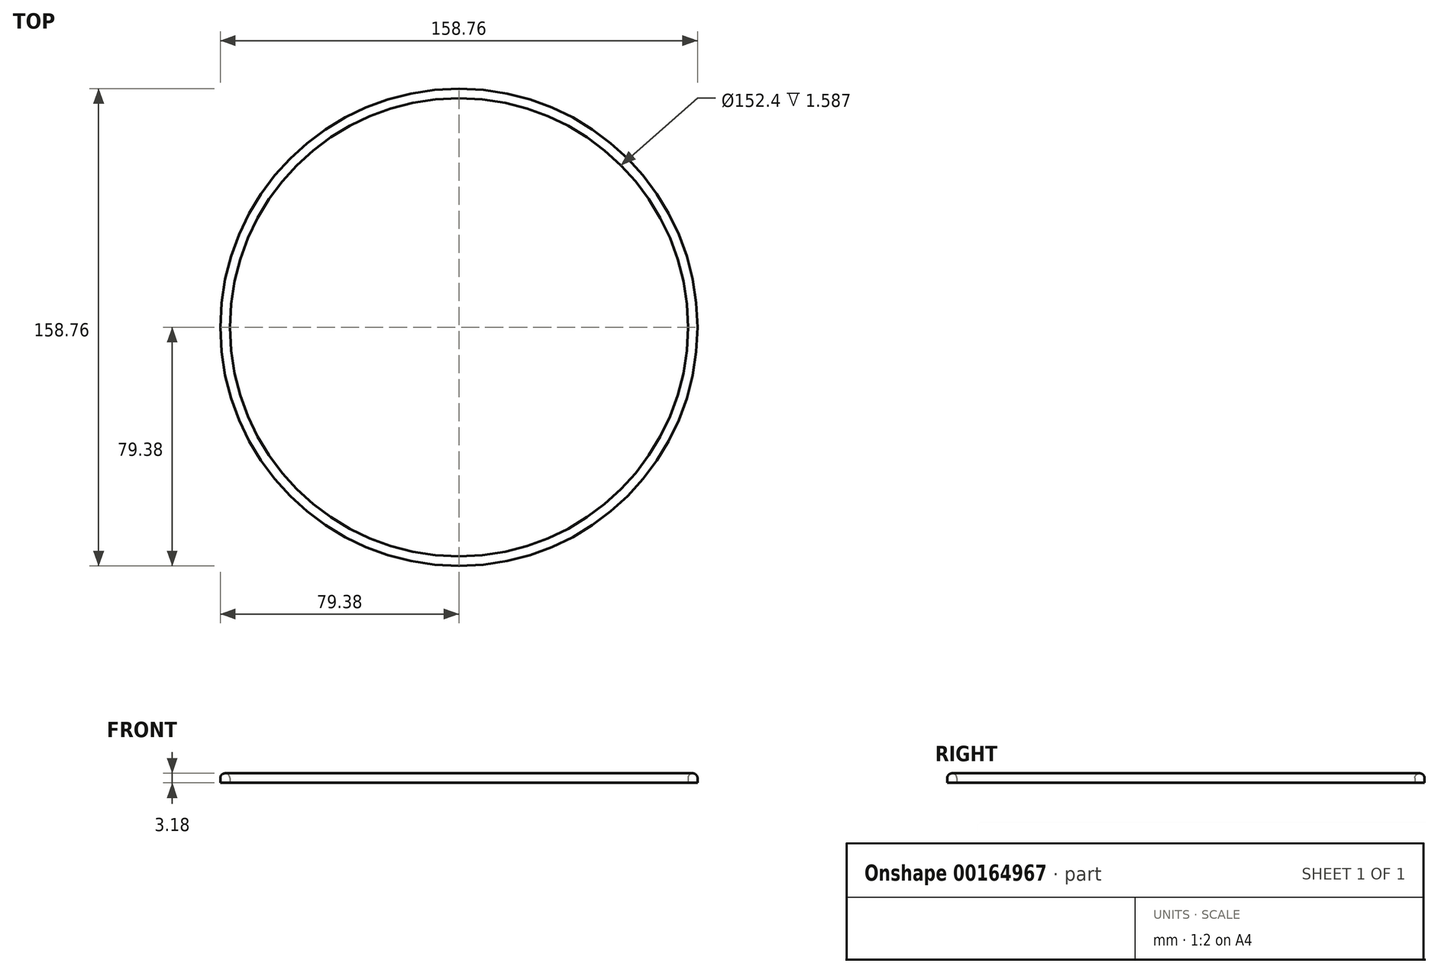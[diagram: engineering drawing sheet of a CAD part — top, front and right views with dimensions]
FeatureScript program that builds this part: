
annotation { "Feature Type Name" : "Feature", "Feature Type Description" : "" }
export const myFeature = defineFeature(function(context is Context, id is Id, definition is map)
    precondition{}
    {
        {
            var Q0;
            Q0=qCreatedBy(makeId("Top.planeOp"),FACE);
            var sketch = newSketch(context, id + "F0", { "sketchPlane" : qUnion([Q0])});
            skCircle(sketch, "E0", {"center": v(0, 0) * mm, "radius": 76.2 * mm});
            skCircle(sketch, "E1", {"center": v(0, 0) * mm, "radius": 79.38 * mm});
            skSolve(sketch);
        }
        {
            var Q0;
            Q0=qSketchRegion(id+"F0",true);
            extrude(context, id + "F1", {"entities" : qUnion([Q0]), "depth" : 3.17 * mm});
        }
        {
            var Q0;
            Q0=makeQuery(id+"F1.opExtrude","CAP_EDGE",EDGE,{"disambiguationData":[OSD([sQuery(id+"F0.wireOp",EDGE,"E0")])],"isStart":false});
            var Q1;
            Q1=makeQuery(id+"F1.opExtrude","CAP_EDGE",EDGE,{"disambiguationData":[OSD([sQuery(id+"F0.wireOp",EDGE,"E1")])],"isStart":false});
            fillet(context, id + "F2", {"entities" : qUnion([Q0, Q1]), "radius" : 1.59 * mm, "tangentPropagation" : true, "allowEdgeOverflow" : false});
        }
    });
